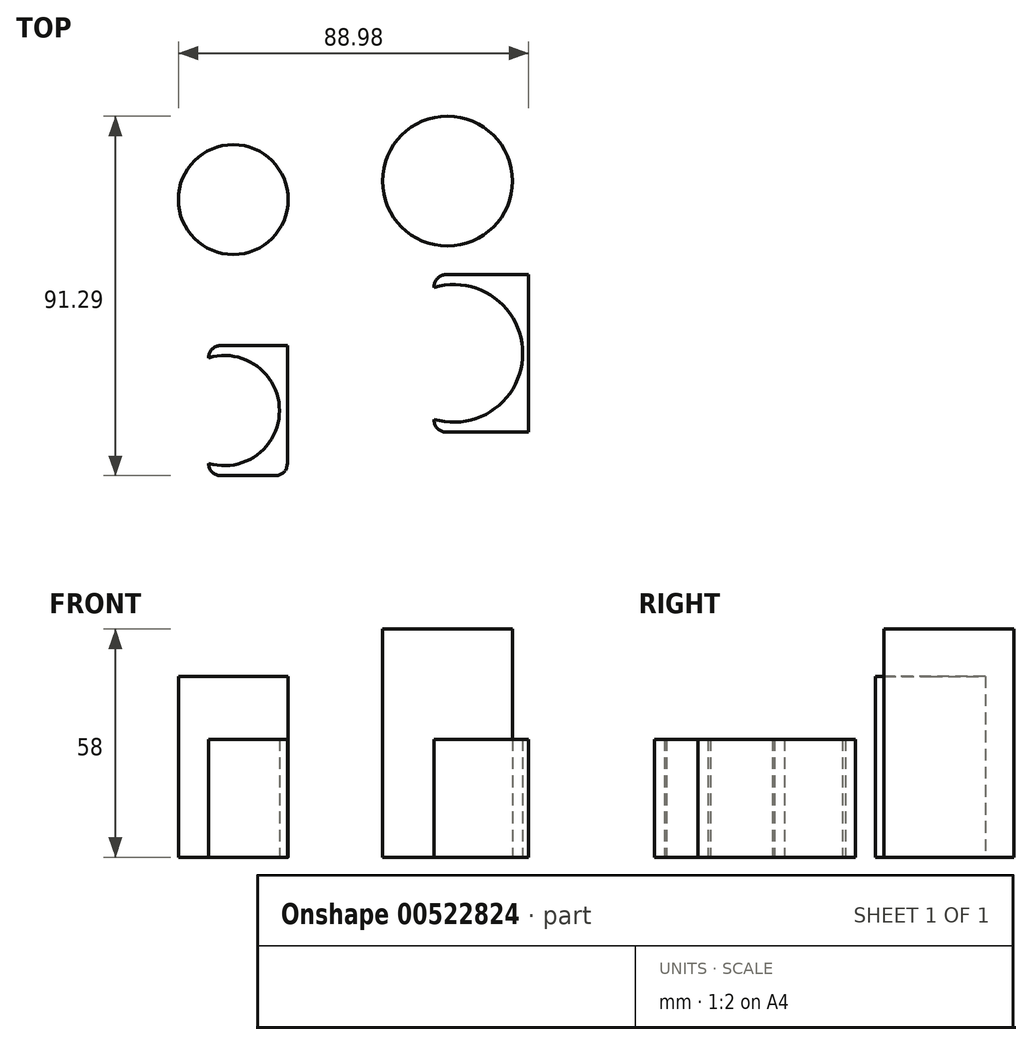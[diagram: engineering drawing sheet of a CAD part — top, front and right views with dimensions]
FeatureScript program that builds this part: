
annotation { "Feature Type Name" : "Feature", "Feature Type Description" : "" }
export const myFeature = defineFeature(function(context is Context, id is Id, definition is map)
    precondition{}
    {
        {
            var Q0;
            Q0=qCreatedBy(makeId("Top.planeOp"),FACE);
            var sketch = newSketch(context, id + "F0", { "sketchPlane" : qUnion([Q0])});
            skCircle(sketch, "E0", {"center": v(-31.99, 22.6) * mm, "radius": 13.95 * mm});
            skCircle(sketch, "E1", {"center": v(22.43, 27.3) * mm, "radius": 16.5 * mm});
            skSolve(sketch);
        }
        {
            var Q0;
            Q0=makeQuery(id+"F0.imprint","IMPRINT",FACE,{"disambiguationData":[TD([[makeQuery(id+"F0.imprint","IMPRINT",EDGE,{"derivedFrom":sQuery(id+"F0.wireOp",EDGE,"E0")}),1.0]])]});
            extrude(context, id + "F1", {"entities" : qUnion([Q0]), "depth" : 46 * mm, "offsetDistance" : 25 * mm});
        }
        {
            var Q0;
            Q0=makeQuery(id+"F0.imprint","IMPRINT",FACE,{"disambiguationData":[TD([[makeQuery(id+"F0.imprint","IMPRINT",EDGE,{"derivedFrom":sQuery(id+"F0.wireOp",EDGE,"E1")}),1.0]])]});
            extrude(context, id + "F2", {"entities" : qUnion([Q0]), "depth" : 58 * mm, "offsetDistance" : 25 * mm});
        }
        {
            var Q0;
            Q0=qCreatedBy(makeId("Top.planeOp"),FACE);
            var sketch = newSketch(context, id + "F3", { "sketchPlane" : qUnion([Q0])});
            skLineSegment(sketch, "E2.bottom", {"start": v(-38.25, -14.5) * mm, "end": v(-18.25, -14.5) * mm});
            skLineSegment(sketch, "E2.top", {"start": v(-38.25, -47.5) * mm, "end": v(-18.25, -47.5) * mm});
            skLineSegment(sketch, "E2.left", {"start": v(-38.25, -14.5) * mm, "end": v(-38.25, -47.5) * mm});
            skLineSegment(sketch, "E2.right", {"start": v(-18.25, -14.5) * mm, "end": v(-18.25, -47.5) * mm});
            skLineSegment(sketch, "E3.bottom", {"start": v(43.04, -36.47) * mm, "end": v(19.04, -36.47) * mm});
            skLineSegment(sketch, "E3.top", {"start": v(43.04, 3.53) * mm, "end": v(19.04, 3.53) * mm});
            skLineSegment(sketch, "E3.left", {"start": v(43.04, -36.47) * mm, "end": v(43.04, 3.53) * mm});
            skLineSegment(sketch, "E3.right", {"start": v(19.04, -36.47) * mm, "end": v(19.04, 3.53) * mm});
            skPoint(sketch, "E3.middle", {"position": v(31.04, -16.47) * mm});
            skLineSegment(sketch, "E4", {"start": v(24.04, 3.53) * mm, "end": v(24.04, -36.47) * mm, "construction": true});
            skCircle(sketch, "E5", {"center": v(24.04, -16.47) * mm, "radius": 17.5 * mm});
            skLineSegment(sketch, "E6", {"start": v(-34.25, -14.5) * mm, "end": v(-34.25, -47.5) * mm, "construction": true});
            skCircle(sketch, "E7", {"center": v(-34.25, -31) * mm, "radius": 14 * mm});
            skSolve(sketch);
        }
        {
            var Q0;
            {var subQ1=sQuery(id+"F3.wireOp",EDGE,"E3.bottom");Q0=makeQuery(id+"F3.imprint","IMPRINT",FACE,{"disambiguationData":[TD([[makeQuery(id+"F3.imprint","IMPRINT",EDGE,{"derivedFrom":subQ1}),-1.0]])]});}
            var Q1;
            {var subQ5=sQuery(id+"F3.wireOp",EDGE,"E2.bottom");Q1=makeQuery(id+"F3.imprint","IMPRINT",FACE,{"disambiguationData":[TD([[makeQuery(id+"F3.imprint","IMPRINT",EDGE,{"derivedFrom":subQ5}),-1.0]])]});}
            extrude(context, id + "F4", {"entities" : qUnion([Q0, Q1]), "depth" : 30 * mm, "offsetDistance" : 25 * mm});
        }
        {
            var Q0;
            Q0=makeQuery(id+"F4.opExtrude","SWEPT_EDGE",EDGE,{"disambiguationData":[OSD([sQuery(id+"F3.wireOp",EDGE,"E2.top"),sQuery(id+"F3.wireOp",EDGE,"E2.left")])]});
            var Q1;
            Q1=makeQuery(id+"F4.opExtrude","SWEPT_EDGE",EDGE,{"disambiguationData":[OSD([sQuery(id+"F3.wireOp",EDGE,"E2.bottom"),sQuery(id+"F3.wireOp",EDGE,"E2.left")])]});
            var Q2;
            Q2=makeQuery(id+"F4.opExtrude","SWEPT_EDGE",EDGE,{"disambiguationData":[OSD([sQuery(id+"F3.wireOp",EDGE,"E3.top"),sQuery(id+"F3.wireOp",EDGE,"E3.right")])]});
            var Q3;
            Q3=makeQuery(id+"F4.opExtrude","SWEPT_EDGE",EDGE,{"disambiguationData":[OSD([sQuery(id+"F3.wireOp",EDGE,"E3.bottom"),sQuery(id+"F3.wireOp",EDGE,"E3.right")])]});
            fillet(context, id + "F5", {"entities" : qUnion([Q0, Q1, Q2, Q3]), "radius" : 3 * mm, "tangentPropagation" : true, "allowEdgeOverflow" : false});
        }
        {
            var Q0;
            Q0=makeQuery(id+"F4.opExtrude","SWEPT_EDGE",EDGE,{"disambiguationData":[OSD([sQuery(id+"F3.wireOp",EDGE,"E2.top"),sQuery(id+"F3.wireOp",EDGE,"E2.right")])]});
            fillet(context, id + "F6", {"entities" : qUnion([Q0]), "radius" : 3 * mm, "tangentPropagation" : true, "allowEdgeOverflow" : false});
        }
    });
